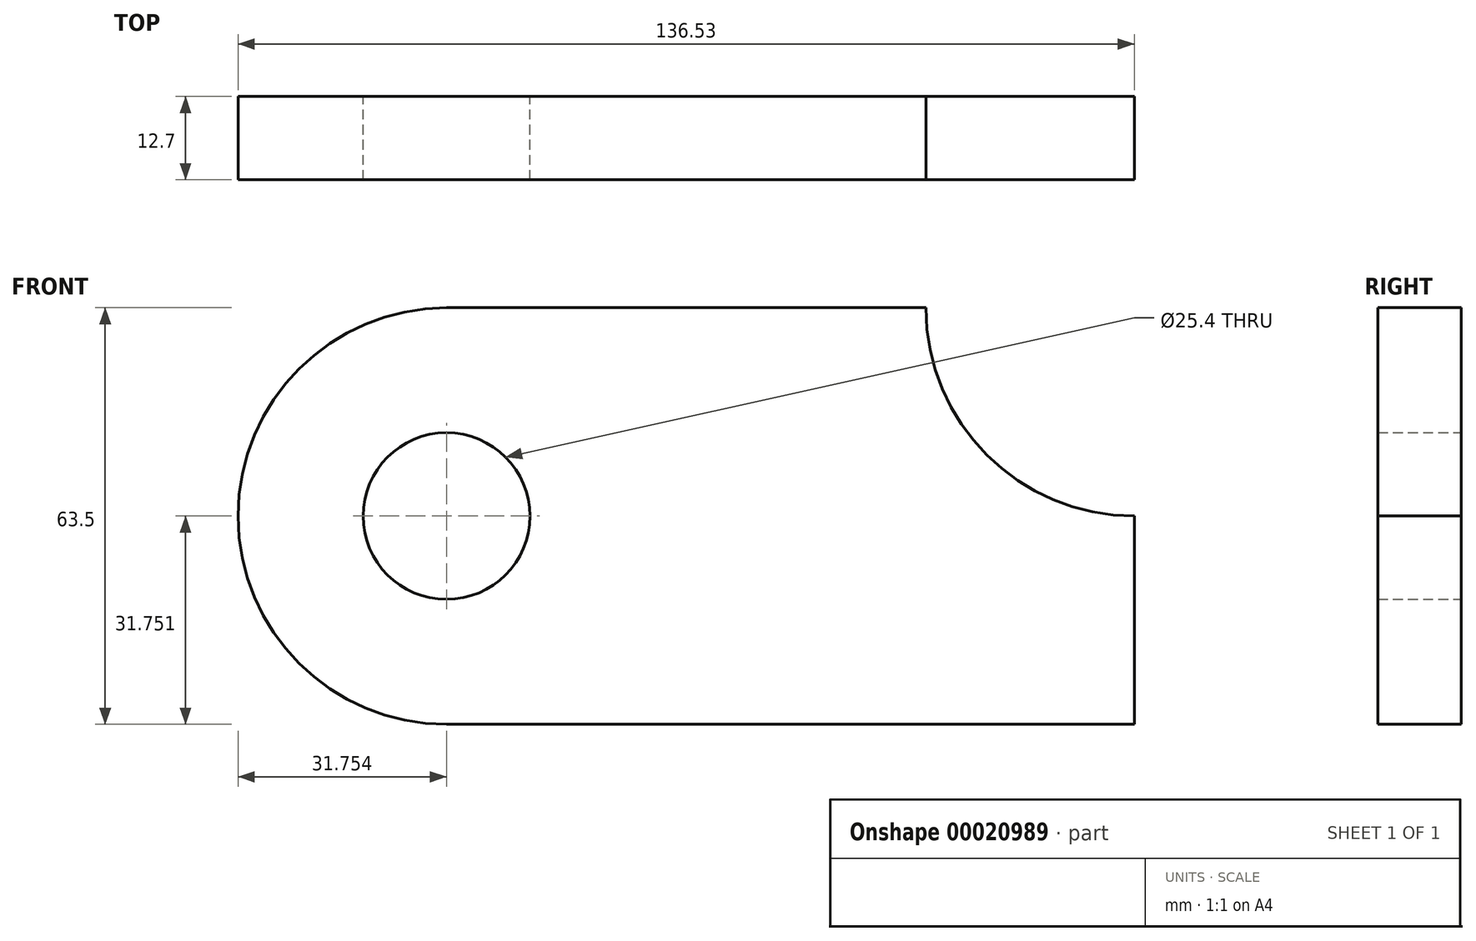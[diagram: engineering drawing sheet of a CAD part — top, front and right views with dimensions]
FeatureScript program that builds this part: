
annotation { "Feature Type Name" : "Feature", "Feature Type Description" : "" }
export const myFeature = defineFeature(function(context is Context, id is Id, definition is map)
    precondition{}
    {
        {
            var Q0;
            Q0=qCreatedBy(makeId("Front.planeOp"),FACE);
            var sketch = newSketch(context, id + "F0", { "sketchPlane" : qUnion([Q0])});
            skLineSegment(sketch, "E0.bottom", {"start": v(-403.43, 80.28) * mm, "end": v(-298.65, 80.28) * mm});
            skLineSegment(sketch, "E0.top", {"start": v(-403.43, 16.78) * mm, "end": v(-298.65, 16.78) * mm});
            skLineSegment(sketch, "E0.left", {"start": v(-403.43, 80.28) * mm, "end": v(-403.43, 16.78) * mm});
            skLineSegment(sketch, "E0.right", {"start": v(-298.65, 80.28) * mm, "end": v(-298.65, 16.78) * mm});
            skCircle(sketch, "E1", {"center": v(-403.43, 48.53) * mm, "radius": 31.75 * mm});
            skCircle(sketch, "E2", {"center": v(-403.43, 48.53) * mm, "radius": 12.7 * mm});
            skPoint(sketch, "E3", {"position": v(-298.65, 48.53) * mm});
            skCircle(sketch, "E4", {"center": v(-298.65, 80.28) * mm, "radius": 31.75 * mm});
            skSolve(sketch);
        }
        {
            var Q0;
            {var subQ6=sQuery(id+"F0.wireOp",EDGE,"E0.top");Q0=makeQuery(id+"F0.imprint","IMPRINT",FACE,{"disambiguationData":[TD([[makeQuery(id+"F0.imprint","IMPRINT",EDGE,{"derivedFrom":subQ6}),1.0]])]});}
            var Q1;
            {var subQ0=sQuery(id+"F0.wireOp",EDGE,"E2");var subQ1=sQuery(id+"F0.wireOp",EDGE,"E0.left");var subQ3=makeQuery(id+"F0.imprint","INTERSECT",VERTEX,{"disambiguationData":[OD(0.0)],"derivedFrom":[subQ1,subQ0]});Q1=makeQuery(id+"F0.imprint","IMPRINT",FACE,{"disambiguationData":[TD([[makeQuery(id+"F0.imprint","IMPRINT",EDGE,{"disambiguationData":[TD([[subQ3,-1.0]])],"derivedFrom":subQ0}),-1.0]])]});}
            var Q2;
            {var subQ0=sQuery(id+"F0.wireOp",EDGE,"E2");var subQ1=sQuery(id+"F0.wireOp",EDGE,"E0.left");var subQ3=makeQuery(id+"F0.imprint","INTERSECT",VERTEX,{"disambiguationData":[OD(0.0)],"derivedFrom":[subQ1,subQ0]});Q2=makeQuery(id+"F0.imprint","IMPRINT",FACE,{"disambiguationData":[TD([[makeQuery(id+"F0.imprint","IMPRINT",EDGE,{"disambiguationData":[TD([[subQ3,1.0]])],"derivedFrom":subQ0}),-1.0]])]});}
            extrude(context, id + "F1", {"entities" : qUnion([Q0, Q1, Q2]), "depth" : 12.7 * mm});
        }
    });
